# Revit family: RN 81034 Optipress-Aquaplus-Übergang
name_source: partatom
category: Rohrformteile
units: mm (PartAtom-declared; Revit-internal decimal feet)

## family parameters
Arbeitsebenenbasiert = Nein
Beim Laden mit Abzugskörper schneiden = Nein
Bemaßung runder Anschluss = Durchmesser verwenden
Gemeinsam genutzt = Nein
Immer vertikal = Ja
Teiletyp = Verbindung

## types (12) — shared parameters
1.010.00.2 Blattnummer der Richtlinie = 29
1.010.00.3 Ausgabedatum (Monat) der Richtlinie = 201308
1.010.00.4 Herstellername = R. Nussbaum AG
1.010.00.5 Revisionsdatum der Datei = 20190521
1.010.00.6 Webadresse des Herstellers = http://www.nussbaum.ch
1.100.00.4 Produktbezeichnung = Versorgung
1.110.00.2 Index = 4
1.110.00.4 Produktbezeichnung = Optipress
1.960/3L.00.8 Link (URL) = https://www.nussbaum.ch
29.700.00.4 Produktname = Optipress-Aquaplus-Übergang, mit Einsteckende und Innengewinde
29.700.00.5 Produktkennung = 2
29.700.00.6 Querschnittsform = 1
29.700.00.7 Nennweitensystem = DN
29.700.00.8 Nenndrucksystem = PN
29.710.02.4 Nenndruck = 16
29.710.02.5 max. zul. Überdruck [hPa] = 1600
29.710.02.7 max. zul. Dauer-Betriebsdruck [hPa] = 1600
29.710.02.9 max. zul. Dauer-Betriebstemperatur [°C] = 95
Connector Visibility = Nein
EnclosingSpace Visibility = Nein

## per-type parameters (varying)
- 81034.21, Optipress-Aquaplus-Übergang, mit Einsteckende und Innengewinde, DN=12x15, L=43, Rp=½: 1.800.00.3 TGA-Nummer=01900400000000000000000000000000000000000000000023000000000000000011; 1.810.00.3 Hersteller-Bestellnummer=81034.21; 1.810.00.4 DATANORM-Nummer=81034.21; 1.810.00.5 StLB-Nummer=267.232; 1.810.00.6 GTIN-Nummer=7612945021502; 29.710.02.10 Formstück-Gewicht [kg]=0.05; 29.710.02.3 Benennung=Optipress-Aquaplus-Übergang, mit Einsteckende und Innengewinde, DN=12x15, L=43, Rp=½; CONNECTOR0_DIAMETER_dX_0r=12 mm  [stored 0.0393701 ft]; CONNECTOR0_dX_01=22 mm; CONNECTOR0_ref_dX=22 mm; CONNECTOR1_DIAMETER_dX_0r=15 mm; CONNECTOR1_dX_00=31 mm; CONNECTOR1_dX_01=44 mm; CONNECTOR1_ref_dX=31 mm; R. Nussbaum AG 81034.20 de Visibility=Nein; R. Nussbaum AG 81034.21 de Visibility=Ja; R. Nussbaum AG 81034.22 de Visibility=Nein; R. Nussbaum AG 81034.23 de Visibility=Nein; R. Nussbaum AG 81034.24 de Visibility=Nein; R. Nussbaum AG 81034.25 de Visibility=Nein; R. Nussbaum AG 81034.28 de Visibility=Nein; R. Nussbaum AG 81034.29 de Visibility=Nein; R. Nussbaum AG 81034.30 de Visibility=Nein; R. Nussbaum AG 81034.31 de Visibility=Nein; R. Nussbaum AG 81034.33 de Visibility=Nein; R. Nussbaum AG 81034.35 de Visibility=Nein
- 81034.22, Optipress-Aquaplus-Übergang, mit Einsteckende und Innengewinde, DN=15, L=43, Rp=½: 1.800.00.3 TGA-Nummer=01900400000000000000000000000000000000000000000023000000000000000012; 1.810.00.3 Hersteller-Bestellnummer=81034.22; 1.810.00.4 DATANORM-Nummer=81034.22; 1.810.00.5 StLB-Nummer=267.233; 1.810.00.6 GTIN-Nummer=7612945021519; 29.710.02.10 Formstück-Gewicht [kg]=0.051; 29.710.02.3 Benennung=Optipress-Aquaplus-Übergang, mit Einsteckende und Innengewinde, DN=15, L=43, Rp=½; CONNECTOR0_DIAMETER_dX_0r=15 mm; CONNECTOR0_dX_01=22 mm; CONNECTOR0_ref_dX=22 mm; CONNECTOR1_DIAMETER_dX_0r=15 mm; CONNECTOR1_dX_00=30 mm; CONNECTOR1_dX_01=43 mm  [stored 0.141076 ft]; CONNECTOR1_ref_dX=30 mm; R. Nussbaum AG 81034.20 de Visibility=Nein; R. Nussbaum AG 81034.21 de Visibility=Nein; R. Nussbaum AG 81034.22 de Visibility=Ja; R. Nussbaum AG 81034.23 de Visibility=Nein; R. Nussbaum AG 81034.24 de Visibility=Nein; R. Nussbaum AG 81034.25 de Visibility=Nein; R. Nussbaum AG 81034.28 de Visibility=Nein; R. Nussbaum AG 81034.29 de Visibility=Nein; R. Nussbaum AG 81034.30 de Visibility=Nein; R. Nussbaum AG 81034.31 de Visibility=Nein; R. Nussbaum AG 81034.33 de Visibility=Nein; R. Nussbaum AG 81034.35 de Visibility=Nein
- 81034.23, Optipress-Aquaplus-Übergang, mit Einsteckende und Innengewinde, DN=15x20, L=45, Rp=¾: 1.800.00.3 TGA-Nummer=01900400000000000000000000000000000000000000000023000000000000000013; 1.810.00.3 Hersteller-Bestellnummer=81034.23; 1.810.00.4 DATANORM-Nummer=81034.23; 1.810.00.6 GTIN-Nummer=7612945021526; 29.710.02.10 Formstück-Gewicht [kg]=0.056; 29.710.02.3 Benennung=Optipress-Aquaplus-Übergang, mit Einsteckende und Innengewinde, DN=15x20, L=45, Rp=¾; CONNECTOR0_DIAMETER_dX_0r=15 mm; CONNECTOR0_dX_01=22 mm; CONNECTOR0_ref_dX=22 mm; CONNECTOR1_DIAMETER_dX_0r=20 mm; CONNECTOR1_dX_00=30 mm; CONNECTOR1_dX_01=45 mm; CONNECTOR1_ref_dX=30 mm; R. Nussbaum AG 81034.20 de Visibility=Nein; R. Nussbaum AG 81034.21 de Visibility=Nein; R. Nussbaum AG 81034.22 de Visibility=Nein; R. Nussbaum AG 81034.23 de Visibility=Ja; R. Nussbaum AG 81034.24 de Visibility=Nein; R. Nussbaum AG 81034.25 de Visibility=Nein; R. Nussbaum AG 81034.28 de Visibility=Nein; R. Nussbaum AG 81034.29 de Visibility=Nein; R. Nussbaum AG 81034.30 de Visibility=Nein; R. Nussbaum AG 81034.31 de Visibility=Nein; R. Nussbaum AG 81034.33 de Visibility=Nein; R. Nussbaum AG 81034.35 de Visibility=Nein
- 81034.24, Optipress-Aquaplus-Übergang, mit Einsteckende und Innengewinde, DN=20x15, L=45, Rp=½: 1.800.00.3 TGA-Nummer=01900400000000000000000000000000000000000000000023000000000000000014; 1.810.00.3 Hersteller-Bestellnummer=81034.24; 1.810.00.4 DATANORM-Nummer=81034.24; 1.810.00.6 GTIN-Nummer=7612945021533; 29.710.02.10 Formstück-Gewicht [kg]=0.064; 29.710.02.3 Benennung=Optipress-Aquaplus-Übergang, mit Einsteckende und Innengewinde, DN=20x15, L=45, Rp=½; CONNECTOR0_DIAMETER_dX_0r=20 mm; CONNECTOR0_dX_01=24 mm; CONNECTOR0_ref_dX=24 mm; CONNECTOR1_DIAMETER_dX_0r=15 mm; CONNECTOR1_dX_00=32 mm; CONNECTOR1_dX_01=45 mm; CONNECTOR1_ref_dX=32 mm; R. Nussbaum AG 81034.20 de Visibility=Nein; R. Nussbaum AG 81034.21 de Visibility=Nein; R. Nussbaum AG 81034.22 de Visibility=Nein; R. Nussbaum AG 81034.23 de Visibility=Nein; R. Nussbaum AG 81034.24 de Visibility=Ja; R. Nussbaum AG 81034.25 de Visibility=Nein; R. Nussbaum AG 81034.28 de Visibility=Nein; R. Nussbaum AG 81034.29 de Visibility=Nein; R. Nussbaum AG 81034.30 de Visibility=Nein; R. Nussbaum AG 81034.31 de Visibility=Nein; R. Nussbaum AG 81034.33 de Visibility=Nein; R. Nussbaum AG 81034.35 de Visibility=Nein
- 81034.25, Optipress-Aquaplus-Übergang, mit Einsteckende und Innengewinde, DN=20, L=47, Rp=¾: 1.800.00.3 TGA-Nummer=01900400000000000000000000000000000000000000000023000000000000000015; 1.810.00.3 Hersteller-Bestellnummer=81034.25; 1.810.00.4 DATANORM-Nummer=81034.25; 1.810.00.5 StLB-Nummer=267.234; 1.810.00.6 GTIN-Nummer=7612945021540; 29.710.02.10 Formstück-Gewicht [kg]=0.081; 29.710.02.3 Benennung=Optipress-Aquaplus-Übergang, mit Einsteckende und Innengewinde, DN=20, L=47, Rp=¾; CONNECTOR0_DIAMETER_dX_0r=20 mm; CONNECTOR0_dX_01=24 mm; CONNECTOR0_ref_dX=24 mm; CONNECTOR1_DIAMETER_dX_0r=20 mm; CONNECTOR1_dX_00=32 mm; CONNECTOR1_dX_01=47 mm; CONNECTOR1_ref_dX=32 mm; R. Nussbaum AG 81034.20 de Visibility=Nein; R. Nussbaum AG 81034.21 de Visibility=Nein; R. Nussbaum AG 81034.22 de Visibility=Nein; R. Nussbaum AG 81034.23 de Visibility=Nein; R. Nussbaum AG 81034.24 de Visibility=Nein; R. Nussbaum AG 81034.25 de Visibility=Ja; R. Nussbaum AG 81034.28 de Visibility=Nein; R. Nussbaum AG 81034.29 de Visibility=Nein; R. Nussbaum AG 81034.30 de Visibility=Nein; R. Nussbaum AG 81034.31 de Visibility=Nein; R. Nussbaum AG 81034.33 de Visibility=Nein; R. Nussbaum AG 81034.35 de Visibility=Nein
- 81034.28, Optipress-Aquaplus-Übergang, mit Einsteckende und Innengewinde, DN=25x20, L=47, Rp=¾: 1.800.00.3 TGA-Nummer=01900400000000000000000000000000000000000000000023000000000000000016; 1.810.00.3 Hersteller-Bestellnummer=81034.28; 1.810.00.4 DATANORM-Nummer=81034.28; 1.810.00.6 GTIN-Nummer=7612945021557; 29.710.02.10 Formstück-Gewicht [kg]=0.086; 29.710.02.3 Benennung=Optipress-Aquaplus-Übergang, mit Einsteckende und Innengewinde, DN=25x20, L=47, Rp=¾; CONNECTOR0_DIAMETER_dX_0r=25 mm  [stored 0.082021 ft]; CONNECTOR0_dX_01=24 mm; CONNECTOR0_ref_dX=24 mm; CONNECTOR1_DIAMETER_dX_0r=20 mm; CONNECTOR1_dX_00=32 mm; CONNECTOR1_dX_01=47 mm; CONNECTOR1_ref_dX=32 mm; R. Nussbaum AG 81034.20 de Visibility=Nein; R. Nussbaum AG 81034.21 de Visibility=Nein; R. Nussbaum AG 81034.22 de Visibility=Nein; R. Nussbaum AG 81034.23 de Visibility=Nein; R. Nussbaum AG 81034.24 de Visibility=Nein; R. Nussbaum AG 81034.25 de Visibility=Nein; R. Nussbaum AG 81034.28 de Visibility=Ja; R. Nussbaum AG 81034.29 de Visibility=Nein; R. Nussbaum AG 81034.30 de Visibility=Nein; R. Nussbaum AG 81034.31 de Visibility=Nein; R. Nussbaum AG 81034.33 de Visibility=Nein; R. Nussbaum AG 81034.35 de Visibility=Nein
- 81034.29, Optipress-Aquaplus-Übergang, mit Einsteckende und Innengewinde, DN=25, L=51, Rp=1: 1.800.00.3 TGA-Nummer=01900400000000000000000000000000000000000000000023000000000000000017; 1.810.00.3 Hersteller-Bestellnummer=81034.29; 1.810.00.4 DATANORM-Nummer=81034.29; 1.810.00.5 StLB-Nummer=267.235; 1.810.00.6 GTIN-Nummer=7612945021564; 29.710.02.10 Formstück-Gewicht [kg]=0.117; 29.710.02.3 Benennung=Optipress-Aquaplus-Übergang, mit Einsteckende und Innengewinde, DN=25, L=51, Rp=1; CONNECTOR0_DIAMETER_dX_0r=25 mm  [stored 0.082021 ft]; CONNECTOR0_dX_01=24 mm; CONNECTOR0_ref_dX=24 mm; CONNECTOR1_DIAMETER_dX_0r=25 mm  [stored 0.082021 ft]; CONNECTOR1_dX_00=34 mm; CONNECTOR1_dX_01=51 mm  [stored 0.167323 ft]; CONNECTOR1_ref_dX=34 mm; R. Nussbaum AG 81034.20 de Visibility=Nein; R. Nussbaum AG 81034.21 de Visibility=Nein; R. Nussbaum AG 81034.22 de Visibility=Nein; R. Nussbaum AG 81034.23 de Visibility=Nein; R. Nussbaum AG 81034.24 de Visibility=Nein; R. Nussbaum AG 81034.25 de Visibility=Nein; R. Nussbaum AG 81034.28 de Visibility=Nein; R. Nussbaum AG 81034.29 de Visibility=Ja; R. Nussbaum AG 81034.30 de Visibility=Nein; R. Nussbaum AG 81034.31 de Visibility=Nein; R. Nussbaum AG 81034.33 de Visibility=Nein; R. Nussbaum AG 81034.35 de Visibility=Nein
- 81034.31, Optipress-Aquaplus-Übergang, mit Einsteckende und Innengewinde, DN=32, L=59, Rp=1¼: 1.800.00.3 TGA-Nummer=01900400000000000000000000000000000000000000000023000000000000000018; 1.810.00.3 Hersteller-Bestellnummer=81034.31; 1.810.00.4 DATANORM-Nummer=81034.31; 1.810.00.5 StLB-Nummer=267.236; 1.810.00.6 GTIN-Nummer=7612945021588; 29.710.02.10 Formstück-Gewicht [kg]=0.171; 29.710.02.3 Benennung=Optipress-Aquaplus-Übergang, mit Einsteckende und Innengewinde, DN=32, L=59, Rp=1¼; CONNECTOR0_DIAMETER_dX_0r=32 mm; CONNECTOR0_dX_01=26 mm; CONNECTOR0_ref_dX=26 mm; CONNECTOR1_DIAMETER_dX_0r=32 mm; CONNECTOR1_dX_00=40 mm  [stored 0.131234 ft]; CONNECTOR1_dX_01=59 mm; CONNECTOR1_ref_dX=40 mm  [stored 0.131234 ft]; R. Nussbaum AG 81034.20 de Visibility=Nein; R. Nussbaum AG 81034.21 de Visibility=Nein; R. Nussbaum AG 81034.22 de Visibility=Nein; R. Nussbaum AG 81034.23 de Visibility=Nein; R. Nussbaum AG 81034.24 de Visibility=Nein; R. Nussbaum AG 81034.25 de Visibility=Nein; R. Nussbaum AG 81034.28 de Visibility=Nein; R. Nussbaum AG 81034.29 de Visibility=Nein; R. Nussbaum AG 81034.30 de Visibility=Nein; R. Nussbaum AG 81034.31 de Visibility=Ja; R. Nussbaum AG 81034.33 de Visibility=Nein; R. Nussbaum AG 81034.35 de Visibility=Nein
- 81034.33, Optipress-Aquaplus-Übergang, mit Einsteckende und Innengewinde, DN=40, L=70, Rp=1½: 1.800.00.3 TGA-Nummer=01900400000000000000000000000000000000000000000023000000000000000019; 1.810.00.3 Hersteller-Bestellnummer=81034.33; 1.810.00.4 DATANORM-Nummer=81034.33; 1.810.00.5 StLB-Nummer=267.237; 1.810.00.6 GTIN-Nummer=7612945021595; 29.710.02.10 Formstück-Gewicht [kg]=0.219; 29.710.02.3 Benennung=Optipress-Aquaplus-Übergang, mit Einsteckende und Innengewinde, DN=40, L=70, Rp=1½; CONNECTOR0_DIAMETER_dX_0r=40 mm  [stored 0.131234 ft]; CONNECTOR0_dX_01=36 mm; CONNECTOR0_ref_dX=36 mm; CONNECTOR1_DIAMETER_dX_0r=40 mm  [stored 0.131234 ft]; CONNECTOR1_dX_00=51 mm  [stored 0.167323 ft]; CONNECTOR1_dX_01=70 mm; CONNECTOR1_ref_dX=51 mm  [stored 0.167323 ft]; R. Nussbaum AG 81034.20 de Visibility=Nein; R. Nussbaum AG 81034.21 de Visibility=Nein; R. Nussbaum AG 81034.22 de Visibility=Nein; R. Nussbaum AG 81034.23 de Visibility=Nein; R. Nussbaum AG 81034.24 de Visibility=Nein; R. Nussbaum AG 81034.25 de Visibility=Nein; R. Nussbaum AG 81034.28 de Visibility=Nein; R. Nussbaum AG 81034.29 de Visibility=Nein; R. Nussbaum AG 81034.30 de Visibility=Nein; R. Nussbaum AG 81034.31 de Visibility=Nein; R. Nussbaum AG 81034.33 de Visibility=Ja; R. Nussbaum AG 81034.35 de Visibility=Nein
- 81034.35, Optipress-Aquaplus-Übergang, mit Einsteckende und Innengewinde, DN=50, L=80, Rp=2: 1.800.00.3 TGA-Nummer=01900400000000000000000000000000000000000000000023000000000000000020; 1.810.00.3 Hersteller-Bestellnummer=81034.35; 1.810.00.4 DATANORM-Nummer=81034.35; 1.810.00.5 StLB-Nummer=267.238; 1.810.00.6 GTIN-Nummer=7612945021601; 29.710.02.10 Formstück-Gewicht [kg]=0.536; 29.710.02.3 Benennung=Optipress-Aquaplus-Übergang, mit Einsteckende und Innengewinde, DN=50, L=80, Rp=2; CONNECTOR0_DIAMETER_dX_0r=50 mm  [stored 0.164042 ft]; CONNECTOR0_dX_01=40 mm  [stored 0.131234 ft]; CONNECTOR0_ref_dX=40 mm  [stored 0.131234 ft]; CONNECTOR1_DIAMETER_dX_0r=50 mm  [stored 0.164042 ft]; CONNECTOR1_dX_00=56 mm; CONNECTOR1_dX_01=80 mm  [stored 0.262467 ft]; CONNECTOR1_ref_dX=56 mm; R. Nussbaum AG 81034.20 de Visibility=Nein; R. Nussbaum AG 81034.21 de Visibility=Nein; R. Nussbaum AG 81034.22 de Visibility=Nein; R. Nussbaum AG 81034.23 de Visibility=Nein; R. Nussbaum AG 81034.24 de Visibility=Nein; R. Nussbaum AG 81034.25 de Visibility=Nein; R. Nussbaum AG 81034.28 de Visibility=Nein; R. Nussbaum AG 81034.29 de Visibility=Nein; R. Nussbaum AG 81034.30 de Visibility=Nein; R. Nussbaum AG 81034.31 de Visibility=Nein; R. Nussbaum AG 81034.33 de Visibility=Nein; R. Nussbaum AG 81034.35 de Visibility=Ja
- 81034.20, Optipress-Aquaplus-Übergang, mit Einsteckende und Innengewinde, DN=10x15, L=40, Rp=½: 1.800.00.3 TGA-Nummer=01900400000000000000000000000000000000000000000023000000000000000021; 1.810.00.3 Hersteller-Bestellnummer=81034.20; 1.810.00.4 DATANORM-Nummer=81034.20; 1.810.00.5 StLB-Nummer=267.231; 1.810.00.6 GTIN-Nummer=7612945021496; 29.710.02.10 Formstück-Gewicht [kg]=0.046; 29.710.02.3 Benennung=Optipress-Aquaplus-Übergang, mit Einsteckende und Innengewinde, DN=10x15, L=40, Rp=½; CONNECTOR0_DIAMETER_dX_0r=20 mm; CONNECTOR0_dX_01=18 mm; CONNECTOR0_ref_dX=18 mm; CONNECTOR1_DIAMETER_dX_0r=15 mm; CONNECTOR1_dX_00=27 mm; CONNECTOR1_dX_01=40 mm  [stored 0.131234 ft]; CONNECTOR1_ref_dX=27 mm; R. Nussbaum AG 81034.20 de Visibility=Ja; R. Nussbaum AG 81034.21 de Visibility=Nein; R. Nussbaum AG 81034.22 de Visibility=Nein; R. Nussbaum AG 81034.23 de Visibility=Nein; R. Nussbaum AG 81034.24 de Visibility=Nein; R. Nussbaum AG 81034.25 de Visibility=Nein; R. Nussbaum AG 81034.28 de Visibility=Nein; R. Nussbaum AG 81034.29 de Visibility=Nein; R. Nussbaum AG 81034.30 de Visibility=Nein; R. Nussbaum AG 81034.31 de Visibility=Nein; R. Nussbaum AG 81034.33 de Visibility=Nein; R. Nussbaum AG 81034.35 de Visibility=Nein
- 81034.30, Optipress-Aquaplus-Übergang, mit Einsteckende und Innengewinde, DN=32x25, L=54, Rp=1: 1.800.00.3 TGA-Nummer=01900400000000000000000000000000000000000000000023000000000000000022; 1.810.00.3 Hersteller-Bestellnummer=81034.30; 1.810.00.4 DATANORM-Nummer=81034.30; 1.810.00.6 GTIN-Nummer=7612945021571; 29.710.02.10 Formstück-Gewicht [kg]=0.115; 29.710.02.3 Benennung=Optipress-Aquaplus-Übergang, mit Einsteckende und Innengewinde, DN=32x25, L=54, Rp=1; CONNECTOR0_DIAMETER_dX_0r=32 mm; CONNECTOR0_dX_01=26 mm; CONNECTOR0_ref_dX=26 mm; CONNECTOR1_DIAMETER_dX_0r=25 mm  [stored 0.082021 ft]; CONNECTOR1_dX_00=37 mm; CONNECTOR1_dX_01=54 mm; CONNECTOR1_ref_dX=37 mm; R. Nussbaum AG 81034.20 de Visibility=Nein; R. Nussbaum AG 81034.21 de Visibility=Nein; R. Nussbaum AG 81034.22 de Visibility=Nein; R. Nussbaum AG 81034.23 de Visibility=Nein; R. Nussbaum AG 81034.24 de Visibility=Nein; R. Nussbaum AG 81034.25 de Visibility=Nein; R. Nussbaum AG 81034.28 de Visibility=Nein; R. Nussbaum AG 81034.29 de Visibility=Nein; R. Nussbaum AG 81034.30 de Visibility=Ja; R. Nussbaum AG 81034.31 de Visibility=Nein; R. Nussbaum AG 81034.33 de Visibility=Nein; R. Nussbaum AG 81034.35 de Visibility=Nein

note: column(s) folded — value = type name in every type: 1.800.00.4 Kommentarfeld

note: [stored X ft] marks values corroborated as IEEE doubles in the binary element streams (Revit-internal decimal feet)

## geometry (parser evidence)
native form markers: Sweep x3
no freeform markers — native parametric forms only
